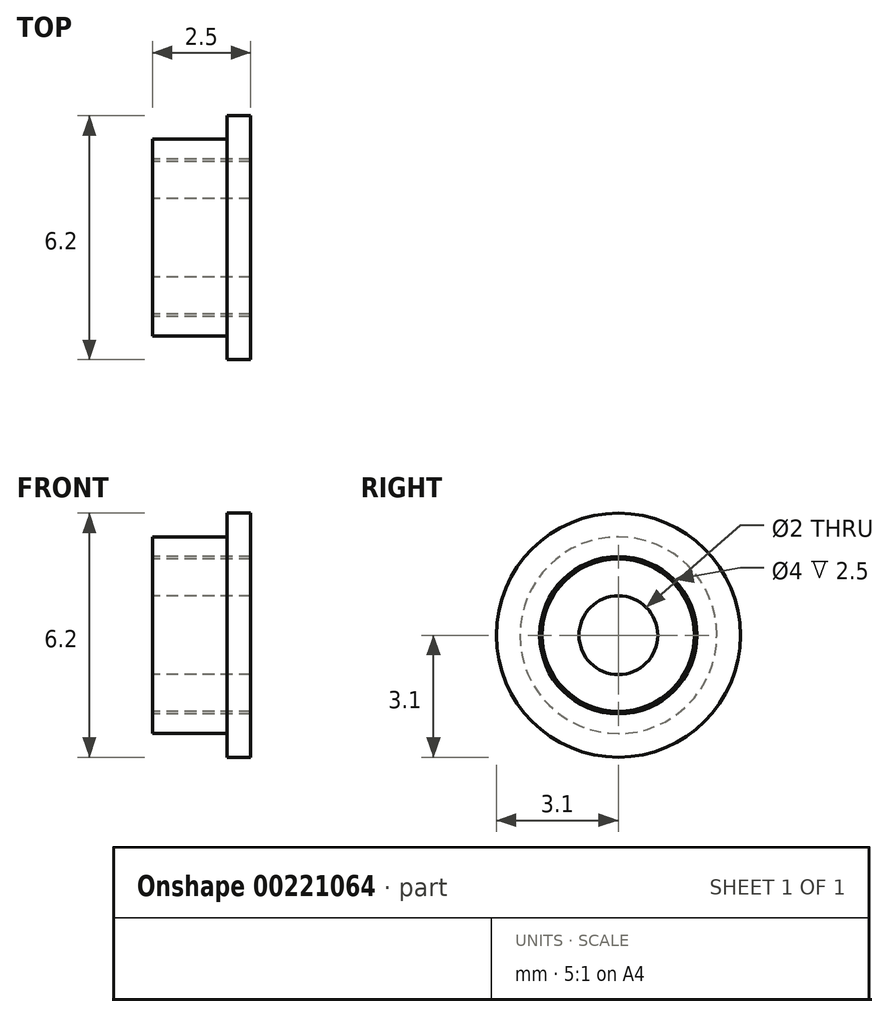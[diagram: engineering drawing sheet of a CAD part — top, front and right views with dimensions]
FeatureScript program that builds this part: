
annotation { "Feature Type Name" : "Feature", "Feature Type Description" : "" }
export const myFeature = defineFeature(function(context is Context, id is Id, definition is map)
    precondition{}
    {
        {
            var Q0;
            Q0=qCreatedBy(makeId("Front.planeOp"),FACE);
            var sketch = newSketch(context, id + "F0", { "sketchPlane" : qUnion([Q0])});
            skLineSegment(sketch, "E0", {"start": v(-1.25, 2.5) * mm, "end": v(-1.25, 2) * mm});
            skLineSegment(sketch, "E1", {"start": v(-1.25, 2) * mm, "end": v(1.25, 2) * mm});
            skLineSegment(sketch, "E2", {"start": v(1.25, 2) * mm, "end": v(1.25, 3.1) * mm});
            skLineSegment(sketch, "E3", {"start": v(1.25, 3.1) * mm, "end": v(0.65, 3.1) * mm});
            skLineSegment(sketch, "E4", {"start": v(0.65, 3.1) * mm, "end": v(0.65, 2.5) * mm});
            skLineSegment(sketch, "E5", {"start": v(0.65, 2.5) * mm, "end": v(-1.25, 2.5) * mm});
            skLineSegment(sketch, "E6", {"start": v(-1.25, 1.94) * mm, "end": v(-1.25, 1) * mm});
            skPoint(sketch, "E6.startSnap0", {"position": v(-1.25, 2.25) * mm});
            skLineSegment(sketch, "E7", {"start": v(-1.25, 1) * mm, "end": v(1.25, 1) * mm});
            skLineSegment(sketch, "E8", {"start": v(1.25, 1) * mm, "end": v(1.25, 1.94) * mm});
            skLineSegment(sketch, "E9", {"start": v(1.25, 1.94) * mm, "end": v(-1.25, 1.94) * mm});
            skLineSegment(sketch, "E10", {"start": v(-1.25, 0) * mm, "end": v(1.25, 0) * mm});
            skSolve(sketch);
        }
        {
            var Q0;
            Q0=makeQuery(id+"F0.imprint","IMPRINT",FACE,{"disambiguationData":[TD([[makeQuery(id+"F0.imprint","IMPRINT",EDGE,{"derivedFrom":sQuery(id+"F0.wireOp",EDGE,"E0")}),1.0]])]});
            var Q1;
            Q1=sQuery(id+"F0.wireOp",EDGE,"E10");
            revolve(context, id + "F1", {"entities" : qUnion([Q0]), "axis" : qUnion([Q1]), "revolveType" : RevolveType.FULL});
        }
        {
            var Q0;
            Q0=makeQuery(id+"F0.imprint","IMPRINT",FACE,{"disambiguationData":[TD([[makeQuery(id+"F0.imprint","IMPRINT",EDGE,{"derivedFrom":sQuery(id+"F0.wireOp",EDGE,"E6")}),1.0]])]});
            var Q1;
            Q1=sQuery(id+"F0.wireOp",EDGE,"E10");
            revolve(context, id + "F2", {"entities" : qUnion([Q0]), "axis" : qUnion([Q1]), "revolveType" : RevolveType.FULL});
        }
    });
